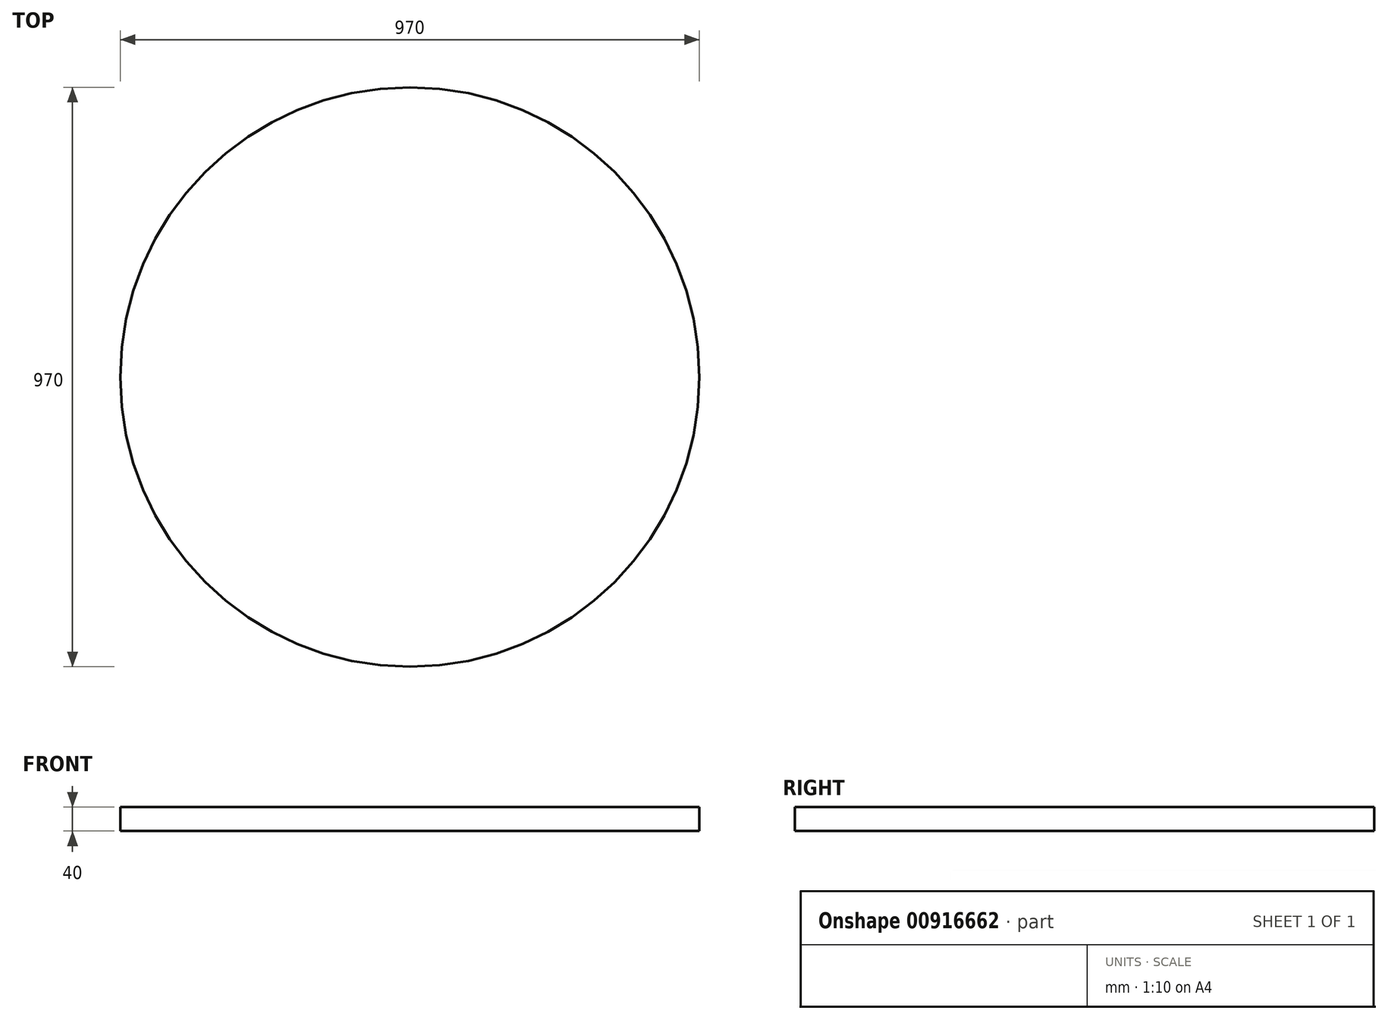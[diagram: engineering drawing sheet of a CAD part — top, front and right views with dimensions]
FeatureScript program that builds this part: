
annotation { "Feature Type Name" : "Feature", "Feature Type Description" : "" }
export const myFeature = defineFeature(function(context is Context, id is Id, definition is map)
    precondition{}
    {
        {
            var Q0;
            Q0=qCreatedBy(makeId("Top.planeOp"),FACE);
            var sketch = newSketch(context, id + "F0", { "sketchPlane" : qUnion([Q0])});
            skCircle(sketch, "E0", {"center": v(0, 0) * mm, "radius": 485 * mm});
            skSolve(sketch);
        }
        {
            var Q0;
            Q0=makeQuery(id+"F0.imprint","IMPRINT",FACE,{"disambiguationData":[TD([[makeQuery(id+"F0.imprint","IMPRINT",EDGE,{"derivedFrom":sQuery(id+"F0.wireOp",EDGE,"E0")}),1.0]])]});
            extrude(context, id + "F1", {"entities" : qUnion([Q0]), "depth" : 40 * mm, "offsetDistance" : 25 * mm});
        }
    });
